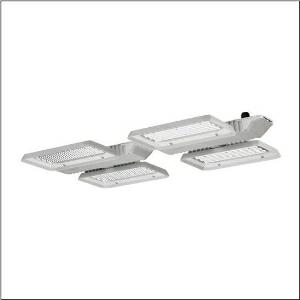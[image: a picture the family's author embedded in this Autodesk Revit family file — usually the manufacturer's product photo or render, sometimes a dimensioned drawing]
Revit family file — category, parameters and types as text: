
# Revit family: highbay_21_51hla2d26mcb
name_source: partatom
category: Lighting Fixtures
units: mm (PartAtom-declared; Revit-internal decimal feet)

## family parameters
Cut with Voids When Loaded = No
Host = Face
Light Source = No
Part Type = Normal
Room Calculation Point = No
Round Connector Dimension = Use Diameter
Shared = No

## types (1)
- --- (1 x LED, 26640 lm, 171.1 W, 6500K)
    Apparent Load = 171 VA
    CIE Flux Codes = 89 96 99 100 100
    Color Rendering = 80
    Color Temperature = 6500K
    Default Elevation = 1800 mm
    Description = Highbay 21, LED high bay luminaire, primary light control with lens, of PMMA, light emission: direct distribution, primary light characteristic: symmetric, installation type: suspended mounting, surface-mounted, for 2x 2 x LED rated luminous flux: 26.640 lm, light colour: 865, colour temperature: 6500K, control gear: ECG DALI, with terminal, 5-pole, max. 2.5mm², mains connection: 230..240V, AC, 50/60Hz, rated input power: 171W, LED unit, of diecast aluminium, unplated, bead blasted, silver, length: 940 mm, width: 500 mm, height: 65mm, housing, of diecast aluminium, uncoated, bead blasted, silver, protection rating (complete): IP65, insulation class (complete): insulation class I (protective earthing), certification: CE, protection symbol: D, impact resistance: IK08 with glass or PC cover, permissible ambient temperature for indoor applications: -35..+45°C, corresponds to IFS (International Featured Standards) requirements for safety and quality in the food industry, reducing of maximum allowable ambient temperature of 5°C with ceiling mounting, packaging unit: 1 piece
    Height = 95 mm
    Lamp = 1 x LED
    Lamp Light Flux = 26640 lm
    Lamp Power = 171.1 W
    Lamp count = 1
    Length = 939 mm
    Luminous efficacy = 156 lm/W
    Manufacturer = Siteco
    ModVariant = No
    Model = 51HLA2D26MCB
    Mounting Place = Ceiling
    Mounting Type = Pendant
    Number of Poles = 1
    OnlyDefault = Yes
    Power Factor = 1
    Product Name = Highbay 21
    Product group = LED high bay luminaire
    ProductGroupID = 903
    Protection Class = Protection class I
    Protection Degree = IP 65
    RLX_Detail_Level = 1
    RlxData = <blob elided: 64233 chars, md5=ebab83de>
    Socket = socket
    Standby Power = 0 W
    System Light Flux = 26640 lm
    System Power = 171 W
    Type Comments = factory setting: luminous flux: 100 % | dim-lin: 254 | 490 mA
    Type Image = l_1003428.jpg
    URL = http://relux.com
    VarID = @adj_135645
    Voltage = 0 V
    Weight = 0.00 kg
    Width = 501 mm

## geometry (parser evidence)
native form markers: Blend x4, Sweep x11
no freeform markers — native parametric forms only
